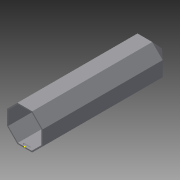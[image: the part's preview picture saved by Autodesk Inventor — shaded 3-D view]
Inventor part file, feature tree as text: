
AUTODESK INVENTOR PART (.ipt)
format: ipt  version: 2015 SP2 (Build 190223200, 223)  size: 189,952 bytes
history: native  units: mm
features: extrude x3, sketch x3, chamfer x2, plane x1, loft x1, shell x1, other x1
ambient origin geometry x8: Origin, YZ Plane, XZ Plane, XY Plane, X Axis, Y Axis, Z Axis, Center Point
bodies: Solid1 (feature_tree)
feature tree (12):
  extrude  "Extrusion1"  Depth=175.0mm TaperAngle=0.0deg
  plane  "Work Plane1"
  loft  "Loft1"
  shell  "Shell2"  Thickness=20.0mm
  sketch  "Sketch8"  dims[d7=0.0mm d8=90.0deg d9=0.0mm d10=90.0deg d13=1.75mm d14=10.0mm d15=2.5mm d16=2.0mm d17=10.0mm d18=2.5mm d19=3.25mm d20=1.0mm d21=0.0mm d22=1.0mm d23=0.0mm d24=1.0mm d25=2.0mm d26=6.108652mm d27=1.0mm d28=2.0mm d29=6.108652mm]
  extrude  "Extrusion2"  TaperAngle=0.0deg  [1 undecoded]
  extrude  "Extrusion3"  Depth=1.0mm
  chamfer  "Chamfer1"  Distance=10.0mm
  chamfer  "Chamfer2"  Distance=2.5mm
  sketch  "Sketch1"  dims[d0=52.0mm d1=175.0mm d2=0.0mm]
  sketch  "Sketch2"  dims[d4=15.0mm d5=20.0mm d6=20.0mm]
  other  "Edges1"
note: 1 required parameter value undecoded (feature->parameter linkage not recoverable at this tier; creation-order binding heuristic only, values carry confidence <= 0.55)
